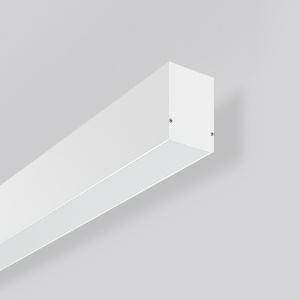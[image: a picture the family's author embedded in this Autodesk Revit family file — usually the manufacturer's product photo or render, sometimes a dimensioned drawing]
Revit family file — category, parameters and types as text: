
# Revit family: less_is_more_50_312607_002_45eb
name_source: partatom
category: Lighting Fixtures
units: mm (PartAtom-declared; Revit-internal decimal feet)

## family parameters
Cut with Voids When Loaded = No
Host = Face
Light Source = No
Part Type = Normal
Room Calculation Point = No
Round Connector Dimension = Use Diameter
Shared = No

## types (1)
- LESS IS MORE 50 (1 x LED Modul 830, 1450 lm, 3000)
    Apparent Load = 12 VA
    CIE Flux Codes = 48 80 96 100 100
    Color Rendering = 80
    Color Temperature = 3000
    Default Elevation = 1800 mm
    Description = Series: LESS IS MORE 50
Linear wall luminaires. Housing: extruded aluminium profile, powder-coated. End cap aluminium powder-coated. Diffuser made of non-yellowing plastic (PMMA), opal. Direct light emission. Suitable for Wall (surface). LED unit with integrated converter interchangeable and removable. Suitable for through-wiring. With sensors or as a safety luminaire on request. 
Colour: traffic white, matt (RAL 9016)
Length: 1127 mm
Width: 67 mm
Height: 75 mm
Lamp: LED
Socket: without socket
Colour temperature: 3000K
Colour rendering index (CRI): 80
System power: 12 W
Rated luminous flux: 1450 lm
Luminous efficiency: 121 lm/W
Control gear: Regulated power supply
Protection class: I
Type of protection: IP 20
    Height = 75 mm
    Lamp = 1 x LED Modul 830
    Lamp Light Flux = 1450 lm
    Lamp count = 1
    Length = 1127 mm
    Lifetime = 50000 h
    Luminous efficacy = 121 lm/W
    Manufacturer = RZB
    ModVariant = No
    Model = 312607.002
    Mounting Place = Wall
    Mounting Type = Surface mounted
    Number of Poles = 1
    OnlyDefault = Yes
    Power Factor = 1
    Product Name = LESS IS MORE 50
    Product group = Surface mounted LED linear luminaires
    ProductGroupID = 2007
    Protection Class = Protection class I
    Protection Degree = IP 20
    RLX_Detail_Level = 1
    RLX_Emergency_Light_Flux = 0 lm
    RLX_Emergency_Type = 0
    RLX_Emergency_Type_DB = No
    RlxData = <blob elided: 35129 chars, md5=2d9931d9>
    Socket = socket
    Standby Power = 0 W
    System Light Flux = 1450 lm
    System Power = 12 W
    Type Comments = Product without accessories
    Type Image = 312606.002.jpg
    URL = http://relux.com
    VarID = ---
    Voltage = 0 V
    Weight = 0.00 kg
    Width = 67 mm

## geometry (parser evidence)
native form markers: Blend x4, Sweep x11
no freeform markers — native parametric forms only
